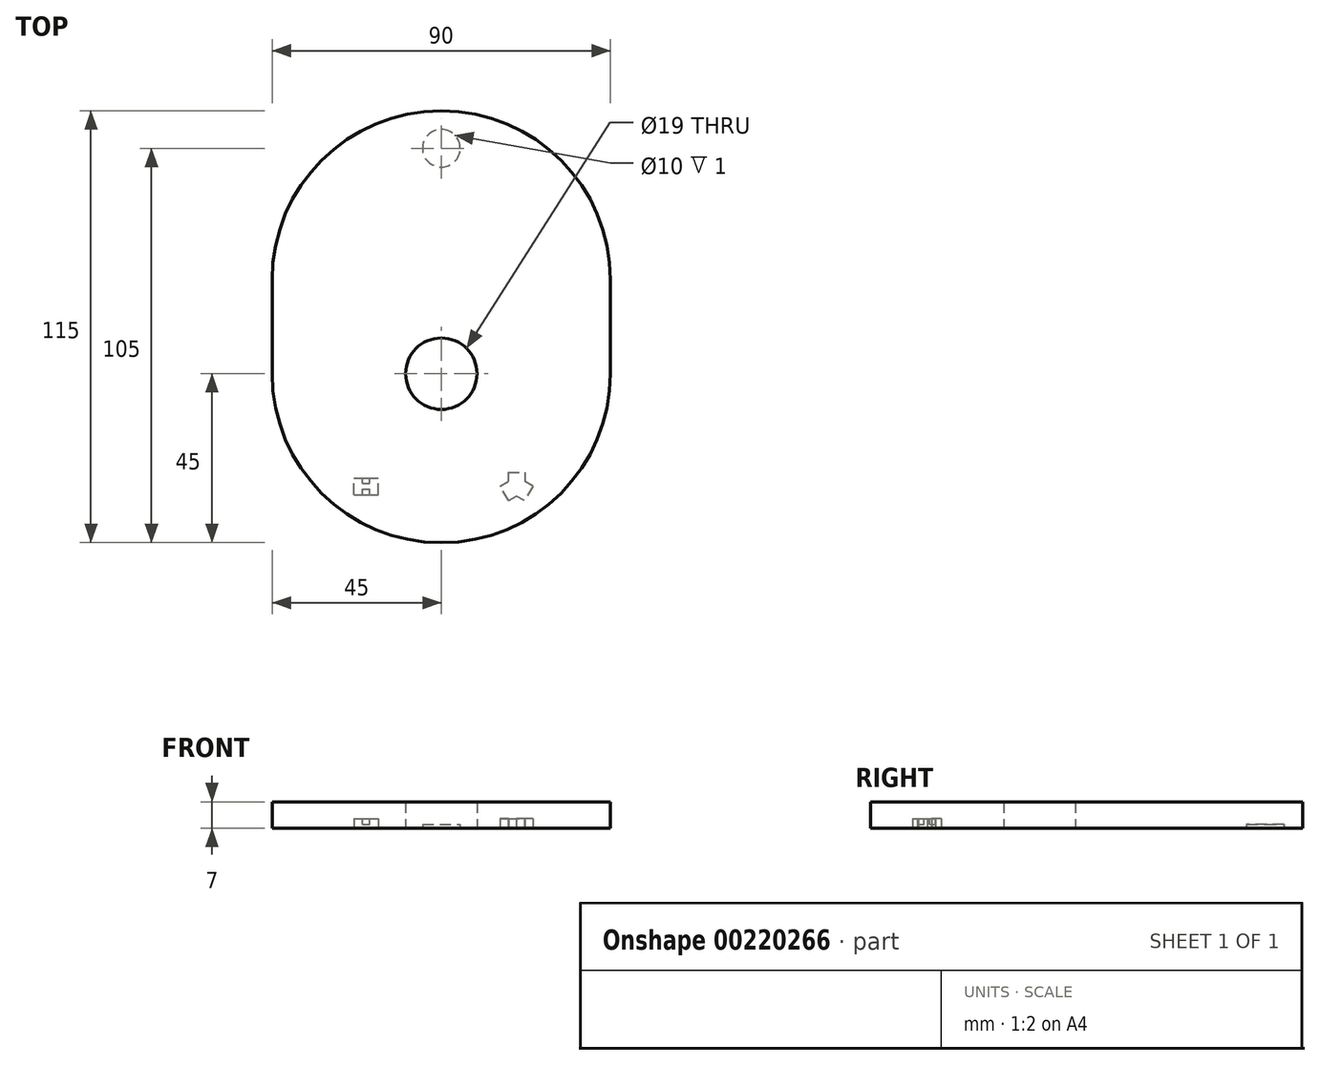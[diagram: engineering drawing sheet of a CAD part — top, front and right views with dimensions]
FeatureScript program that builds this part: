
annotation { "Feature Type Name" : "Feature", "Feature Type Description" : "" }
export const myFeature = defineFeature(function(context is Context, id is Id, definition is map)
    precondition{}
    {
        {
            var Q0;
            Q0=qCreatedBy(makeId("Top.planeOp"),FACE);
            var sketch = newSketch(context, id + "F0", { "sketchPlane" : qUnion([Q0])});
            skArc(sketch, "E0", {"start": v(-45, 0) * mm, "mid": v(0, -45) * mm, "end": v(45, 0) * mm});
            skLineSegment(sketch, "E1", {"start": v(-45, 0) * mm, "end": v(-45, 70) * mm});
            skLineSegment(sketch, "E2", {"start": v(-45, 70) * mm, "end": v(45, 70) * mm});
            skLineSegment(sketch, "E3", {"start": v(45, 70) * mm, "end": v(45, 0) * mm});
            skSolve(sketch);
        }
        {
            var Q0;
            Q0=qSketchRegion(id+"F0",true);
            extrude(context, id + "F1", {"entities" : qUnion([Q0]), "depth" : 7 * mm});
        }
        {
            var Q0;
            Q0=makeQuery(id+"F1.opExtrude","CAP_FACE",FACE,{"disambiguationData":[OSD([sQuery(id+"F0.wireOp",EDGE,"E0")])],"isStart":true});
            var sketch = newSketch(context, id + "F2", { "sketchPlane" : qUnion([Q0])});
            skCircle(sketch, "E4", {"center": v(0, 0) * mm, "radius": 9.5 * mm});
            skSolve(sketch);
        }
        {
            var Q0;
            Q0=qSketchRegion(id+"F2",true);
            extrude(context, id + "F3", {"entities" : qUnion([Q0]), "operationType" : NewBodyOperationType.REMOVE, "oppositeDirection" : true, "depth" : 10 * mm});
        }
        {
            var Q0;
            Q0=makeQuery(id+"F1.opExtrude","CAP_FACE",FACE,{"disambiguationData":[OSD([sQuery(id+"F0.wireOp",EDGE,"E0")])],"isStart":true});
            var sketch = newSketch(context, id + "F4", { "sketchPlane" : qUnion([Q0])});
            skCircle(sketch, "E5", {"center": v(0, -60) * mm, "radius": 5 * mm});
            skSolve(sketch);
        }
        {
            var Q0;
            Q0=makeQuery(id+"F1.opExtrude","CAP_FACE",FACE,{"disambiguationData":[OSD([sQuery(id+"F0.wireOp",EDGE,"E0"),sQuery(id+"F0.wireOp",EDGE,"E1"),sQuery(id+"F0.wireOp",EDGE,"E2"),sQuery(id+"F0.wireOp",EDGE,"E3")])],"isStart":true});
            var sketch = newSketch(context, id + "F5", { "sketchPlane" : qUnion([Q0])});
            skPoint(sketch, "E6", {"position": v(20, 30) * mm});
            skLineSegment(sketch, "E7", {"start": v(17.88, 33.83) * mm, "end": v(15.63, 29.93) * mm});
            skLineSegment(sketch, "E8", {"start": v(17.75, 26.25) * mm, "end": v(22.25, 26.25) * mm});
            skLineSegment(sketch, "E9", {"start": v(24.37, 29.93) * mm, "end": v(22.12, 33.83) * mm});
            skLineSegment(sketch, "E10", {"start": v(15.62, 29.93) * mm, "end": v(17.75, 28.7) * mm});
            skLineSegment(sketch, "E11", {"start": v(17.87, 33.83) * mm, "end": v(20, 32.6) * mm});
            skLineSegment(sketch, "E12", {"start": v(17.75, 26.25) * mm, "end": v(17.75, 28.7) * mm});
            skLineSegment(sketch, "E13", {"start": v(22.25, 26.25) * mm, "end": v(22.25, 28.7) * mm});
            skLineSegment(sketch, "E14", {"start": v(22.12, 33.83) * mm, "end": v(20, 32.6) * mm});
            skLineSegment(sketch, "E15", {"start": v(24.38, 29.93) * mm, "end": v(22.25, 28.7) * mm});
            skPoint(sketch, "E16.orphan", {"position": v(26.5, 26.25) * mm});
            skPoint(sketch, "E17.orphan", {"position": v(20, 37.5) * mm});
            skPoint(sketch, "E18.orphan", {"position": v(13.5, 26.25) * mm});
            skSolve(sketch);
        }
        {
            var Q0;
            Q0=qSketchRegion(id+"F5",true);
            extrude(context, id + "F6", {"entities" : qUnion([Q0]), "operationType" : NewBodyOperationType.REMOVE, "oppositeDirection" : true, "depth" : 2.5 * mm});
        }
        {
            var Q0;
            Q0=qSketchRegion(id+"F4",true);
            extrude(context, id + "F7", {"entities" : qUnion([Q0]), "operationType" : NewBodyOperationType.REMOVE, "oppositeDirection" : true, "depth" : 1 * mm});
        }
        {
            var Q0;
            Q0=makeQuery(id+"F1.opExtrude","CAP_FACE",FACE,{"disambiguationData":[OSD([sQuery(id+"F0.wireOp",EDGE,"E0"),sQuery(id+"F0.wireOp",EDGE,"E1"),sQuery(id+"F0.wireOp",EDGE,"E2"),sQuery(id+"F0.wireOp",EDGE,"E3")])],"isStart":true});
            var sketch = newSketch(context, id + "F8", { "sketchPlane" : qUnion([Q0])});
            skPoint(sketch, "E19", {"position": v(-20, 30) * mm});
            skLineSegment(sketch, "E20.bottom", {"start": v(-23.25, 32.25) * mm, "end": v(-16.75, 32.25) * mm});
            skLineSegment(sketch, "E20.top", {"start": v(-23.25, 27.75) * mm, "end": v(-16.75, 27.75) * mm});
            skLineSegment(sketch, "E20.left", {"start": v(-23.25, 32.25) * mm, "end": v(-23.25, 27.75) * mm});
            skLineSegment(sketch, "E20.right", {"start": v(-16.75, 32.25) * mm, "end": v(-16.75, 27.75) * mm});
            skSolve(sketch);
        }
        {
            var Q0;
            Q0=qSketchRegion(id+"F8",true);
            extrude(context, id + "F9", {"entities" : qUnion([Q0]), "operationType" : NewBodyOperationType.REMOVE, "oppositeDirection" : true, "depth" : 2.5 * mm});
        }
        {
            var Q0;
            Q0=makeQuery(id+"F9.boolean.opBoolean","COPY",FACE,{"derivedFrom":makeQuery(id+"F9.opExtrude","CAP_FACE",FACE,{"disambiguationData":[OSD([sQuery(id+"F8.wireOp",EDGE,"E20.bottom"),sQuery(id+"F8.wireOp",EDGE,"E20.top"),sQuery(id+"F8.wireOp",EDGE,"E20.left"),sQuery(id+"F8.wireOp",EDGE,"E20.right")])],"isStart":false})});
            var sketch = newSketch(context, id + "F10", { "sketchPlane" : qUnion([Q0])});
            skLineSegment(sketch, "E21.bottom", {"start": v(-21, 32.25) * mm, "end": v(-19, 32.25) * mm});
            skLineSegment(sketch, "E21.top", {"start": v(-21, 27.75) * mm, "end": v(-19, 27.75) * mm});
            skLineSegment(sketch, "E21.left", {"start": v(-21, 32.25) * mm, "end": v(-21, 30.75) * mm});
            skLineSegment(sketch, "E21.right", {"start": v(-19, 32.25) * mm, "end": v(-19, 30.75) * mm});
            skLineSegment(sketch, "E22", {"start": v(-21, 30.75) * mm, "end": v(-19, 30.75) * mm});
            skLineSegment(sketch, "E23", {"start": v(-21, 29.25) * mm, "end": v(-19, 29.25) * mm});
            skLineSegment(sketch, "E24.trimOffspring", {"start": v(-21, 29.25) * mm, "end": v(-21, 27.75) * mm});
            skLineSegment(sketch, "E25.trimOffspring", {"start": v(-19, 29.25) * mm, "end": v(-19, 27.75) * mm});
            skSolve(sketch);
        }
        {
            var Q0;
            Q0=qSketchRegion(id+"F10",true);
            extrude(context, id + "F11", {"entities" : qUnion([Q0]), "operationType" : NewBodyOperationType.ADD, "depth" : 1.5 * mm});
        }
        {
            var Q0;
            Q0=makeQuery(id+"F1.opExtrude","SWEPT_EDGE",EDGE,{"disambiguationData":[OSD([sQuery(id+"F0.wireOp",EDGE,"E1"),sQuery(id+"F0.wireOp",EDGE,"E2")])]});
            var Q1;
            Q1=makeQuery(id+"F1.opExtrude","SWEPT_EDGE",EDGE,{"disambiguationData":[OSD([sQuery(id+"F0.wireOp",EDGE,"E2"),sQuery(id+"F0.wireOp",EDGE,"E3")])]});
            fillet(context, id + "F12", {"entities" : qUnion([Q0, Q1]), "radius" : 45 * mm, "tangentPropagation" : true, "allowEdgeOverflow" : false});
        }
    });
